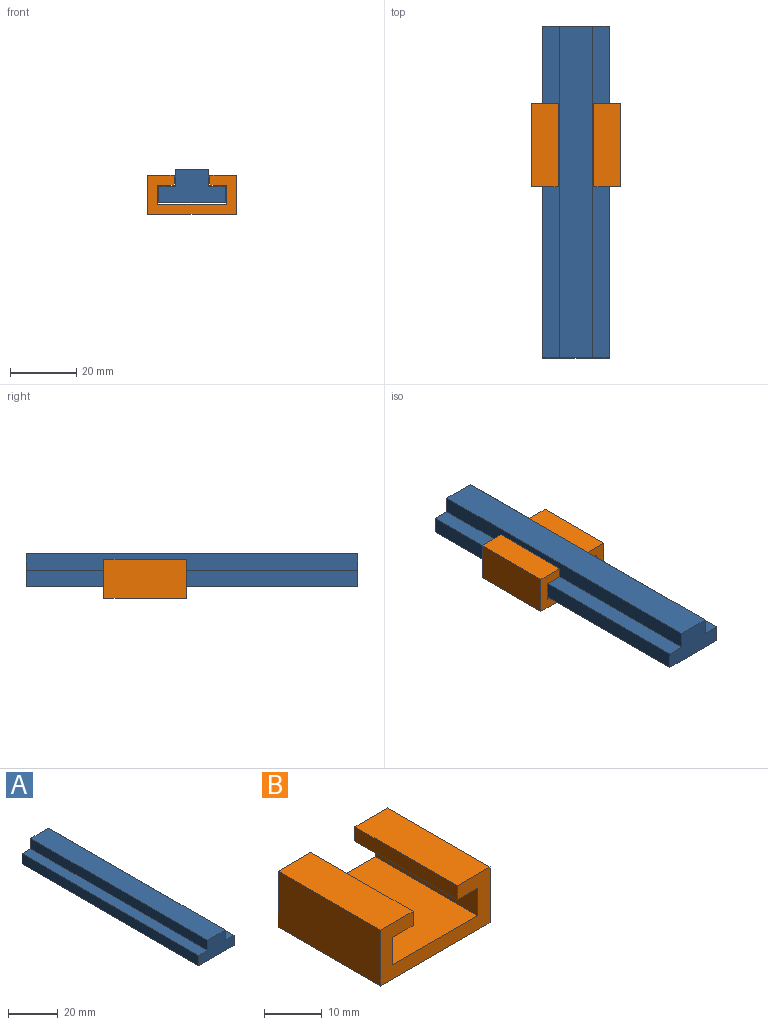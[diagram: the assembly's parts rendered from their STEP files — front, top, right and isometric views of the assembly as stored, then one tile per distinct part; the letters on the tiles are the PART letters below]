
ASSEMBLY  parts=2 mates=1
PART A: 10 faces, bbox 20x100x10 mm
  f0: plane 100x5mm, normal (0,0,1), area 500mm2, adj f1,f7,f8,f9
  f1: plane 100x5mm, normal (-1,0,0), area 500mm2, adj f0,f2,f8,f9
  f2: plane 100x20mm, normal (0,0,-1), area 2000mm2, adj f1,f3,f8,f9
  f3: plane 100x5mm, normal (1,0,0), area 500mm2, adj f2,f4,f8,f9
  f4: plane 100x5mm, normal (0,0,1), area 500mm2, adj f3,f5,f8,f9
  f5: plane 100x5mm, normal (1,0,0), area 500mm2, adj f4,f6,f8,f9
  f6: plane 100x10mm, normal (0,0,1), area 1000mm2, adj f5,f7,f8,f9
  f7: plane 100x5mm, normal (-1,0,0), area 500mm2, adj f0,f6,f8,f9
  f8: plane 20x10mm, normal (0,-1,0), area 150mm2, adj f0,f1,f2,f3,f4,f5,f6,f7
  f9: plane 20x10mm, normal (0,1,0), area 150mm2, adj f0,f1,f2,f3,f4,f5,f6,f7
PART B: 14 faces, bbox 26.8x25x11.8 mm
  f0: plane 25x5.8mm, normal (1,0,0), area 145mm2, adj f1,f11,f12,f13
  f1: plane 25x5mm, normal (0,0,-1), area 125mm2, adj f0,f2,f12,f13
  f2: plane 25x3mm, normal (1,0,0), area 75mm2, adj f1,f3,f12,f13
  f3: plane 25x8mm, normal (0,0,1), area 200mm2, adj f2,f4,f12,f13
  f4: plane 25x11.8mm, normal (-1,0,0), area 295mm2, adj f3,f5,f12,f13
  f5: plane 26.8x25mm, normal (0,0,-1), area 670mm2, adj f4,f6,f12,f13
  f6: plane 25x11.8mm, normal (1,0,0), area 295mm2, adj f5,f7,f12,f13
  f7: plane 25x8mm, normal (0,0,1), area 200mm2, adj f6,f8,f12,f13
  f8: plane 25x3mm, normal (-1,0,0), area 75mm2, adj f7,f9,f12,f13
  f9: plane 25x5mm, normal (0,0,-1), area 125mm2, adj f8,f10,f12,f13
  f10: plane 25x5.8mm, normal (-1,0,0), area 145mm2, adj f9,f11,f12,f13
  f11: plane 25x20.8mm, normal (0,0,1), area 520mm2, adj f0,f10,f12,f13
  f12: plane 26.8x11.8mm, normal (0,-1,0), area 163.2mm2, adj f0,f1,f2,f3,f4,f5,f6,f7
  f13: plane 26.8x11.8mm, normal (0,1,0), area 163.2mm2, adj f0,f1,f2,f3,f4,f5,f6,f7
PLACE A t=(-24.97,39.12,0.31)mm fixed
PLACE B t=(-24.97,15.67,0.31)mm
MATE slider A.f9 <-> B.f13  axis (0,1,0) through (-24.97,39.12,0.31)mm
